# Revit family: ШУЗ-С300
name_source: partatom
category: Оборудование
units: mm (PartAtom-declared; Revit-internal decimal feet)

## family parameters
Всегда вертикально = Да
Классификация = Нет
На основе рабочей плоскости = Нет
Общий = Нет
При загрузке вырезать с полостями = Нет
Размер круглого соединителя = Использовать диаметр
Тип детали = Нормальный
Точка расчета площади = Нет

## types (1)
- ШУЗ-М/IP54/АВВ
    URL = https://plazma-t.ru
    Группа модели = ШУЗ-С300
    Изготовитель = ООО "Плазма-Т"
    Комментарии к типоразмеру = Ш1/ABB
    Назв ПУШ = 120 мм
    Описание = ШУЗ-С300 предназначен для управления одно/трехфазным электроприводом задвижки практически любого производителя из известных на рынке. Управление осуществляется посредством интегрированного модуля контроля и управления МС322-24, что позволяет использовать шкаф в составе Системы пожарной автоматики и сигнализации «СПРУТ-2», в частности – в составе адресно-аналоговой сигнализации «С300».
    Отметка по умолчанию = 0 мм
    Расст ПУШ = 30 мм
    Расст ввод = 220 мм
    Расст ввод 2 = 100 мм
    Расст замок = 260 мм
    выход 3 = Да
    расст вывод = 100 мм
